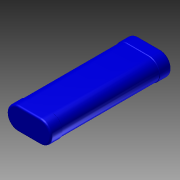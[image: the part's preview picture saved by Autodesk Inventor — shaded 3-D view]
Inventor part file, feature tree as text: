
AUTODESK INVENTOR PART (.ipt)
format: ipt  version: 2013 (Build 170138000, 138)  size: 132,608 bytes
history: native  units: in
note: dims shown in document units (in); Inventor stores cm internally (conversion verified against a paired STEP export)
features: extrude x3, sketch x3, fillet x2, chamfer x1, mirror x1
ambient origin geometry x8: Origin, YZ Plane, XZ Plane, XY Plane, X Axis, Y Axis, Z Axis, Center Point
bodies: Solid1 (feature_tree)
feature tree (10):
  extrude  "Extrusion1"  Depth=0.51in TaperAngle=0.0deg
  extrude  "Extrusion2"  Depth=0.02in TaperAngle=45.0deg
  fillet  "Fillet1"  Radius=0.075in
  chamfer  "Chamfer1"  [1 undecoded]
  mirror  "Mirror1"
  extrude  "Extrusion3"  [1 undecoded]
  fillet  "Fillet2"  [1 undecoded]
  sketch  "Sketch1"  dims[d0=4.15in d1=0.0in d2=0.51in d3=0.0in]
  sketch  "Sketch2"  dims[d4=0.08in d5=0.02in d6=0.125in d7=45.0deg d8=0.075in d9=-0.2061in]
  sketch  "Sketch3"  dims[d10=0.025in]
note: 3 required parameter values undecoded (feature->parameter linkage not recoverable at this tier; creation-order binding heuristic only, values carry confidence <= 0.55)
